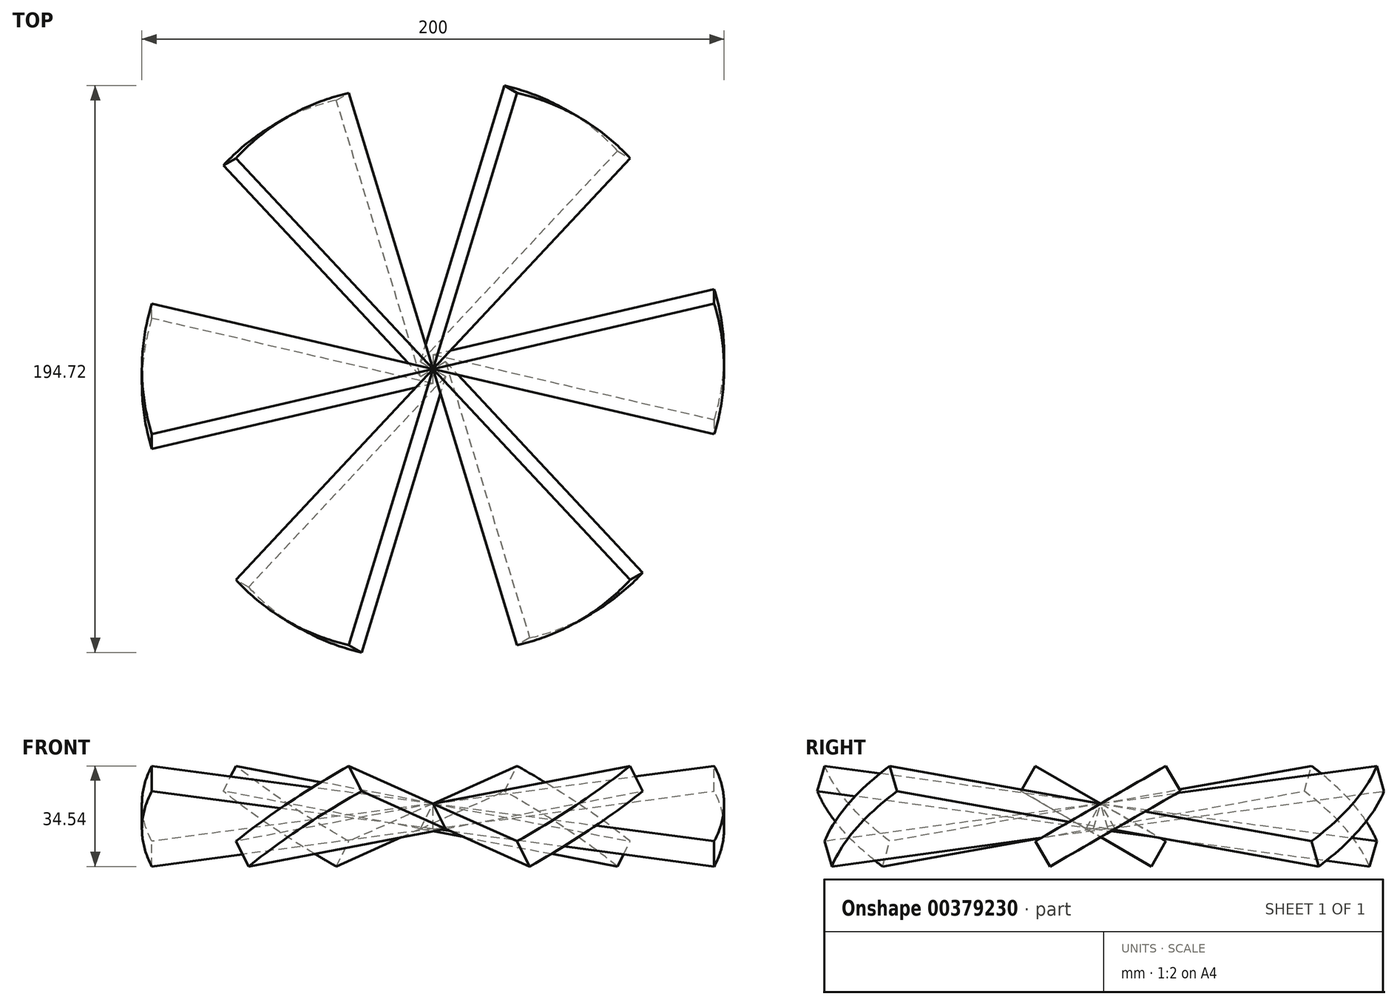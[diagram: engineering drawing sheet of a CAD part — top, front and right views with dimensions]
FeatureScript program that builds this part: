
annotation { "Feature Type Name" : "Feature", "Feature Type Description" : "" }
export const myFeature = defineFeature(function(context is Context, id is Id, definition is map)
    precondition{}
    {
        {
            var Q0;
            Q0=qCreatedBy(makeId("Top.planeOp"),FACE);
            var sketch = newSketch(context, id + "F0", { "sketchPlane" : qUnion([Q0])});
            skLineSegment(sketch, "E0", {"start": v(0, 0) * mm, "end": v(96.6, 25.88) * mm});
            skLineSegment(sketch, "E1", {"start": v(0, 0) * mm, "end": v(96.6, -25.88) * mm});
            skArc(sketch, "E2", {"start": v(96.6, 25.88) * mm, "mid": v(100, 0) * mm, "end": v(96.6, -25.88) * mm});
            skSolve(sketch);
        }
        {
            var Q0;
            Q0=makeQuery(id+"F0.imprint","IMPRINT",FACE,{"disambiguationData":[TD([[makeQuery(id+"F0.imprint","IMPRINT",EDGE,{"derivedFrom":sQuery(id+"F0.wireOp",EDGE,"E0")}),-1.0]])]});
            extrude(context, id + "F1", {"entities" : qUnion([Q0]), "oppositeDirection" : true, "depth" : 10 * mm});
        }
        {
            var Q0;
            Q0=qCreatedBy(makeId("Top.planeOp"),FACE);
            var sketch = newSketch(context, id + "F2", { "sketchPlane" : qUnion([Q0])});
            skLineSegment(sketch, "E3", {"start": v(0, 0) * mm, "end": v(115.1, 0) * mm, "construction": true});
            skSolve(sketch);
        }
        {
            var Q0;
            Q0=makeQuery(id+"F1.opExtrude","SWEPT_BODY",BODY,{"disambiguationData":[OSD([sQuery(id+"F0.wireOp",EDGE,"E0"),sQuery(id+"F0.wireOp",EDGE,"E1"),sQuery(id+"F0.wireOp",EDGE,"E2")])]});
            var Q1;
            Q1=sQuery(id+"F2.wireOp",EDGE,"E3");
            var Q2;
            Q2=sQuery(id+"F2.wireOp",EDGE,"E3");
            transform(context, id + "F3", {"entities" : qUnion([Q0]), "transformType" : TransformType.ROTATION, "transformAxis" : qUnion([Q2]), "angle" : 30 * degree, "makeCopy" : false});
        }
        {
            var Q0;
            Q0=qCreatedBy(makeId("Right.planeOp"),FACE);
            var sketch = newSketch(context, id + "F4", { "sketchPlane" : qUnion([Q0])});
            skLineSegment(sketch, "E4", {"start": v(0, 0) * mm, "end": v(0, 82.27) * mm, "construction": true});
            skSolve(sketch);
        }
        {
            var Q0;
            Q0=makeQuery(id+"F1.opExtrude","SWEPT_BODY",BODY,{"disambiguationData":[OSD([sQuery(id+"F0.wireOp",EDGE,"E0"),sQuery(id+"F0.wireOp",EDGE,"E1"),sQuery(id+"F0.wireOp",EDGE,"E2")])]});
            var Q1;
            Q1=sQuery(id+"F4.wireOp",EDGE,"E4");
            circularPattern(context, id + "F5", {"entities" : qUnion([Q0]), "axis" : qUnion([Q1]), "angle" : 360 * degree, "instanceCount" : 6, "equalSpace" : true});
        }
    });
